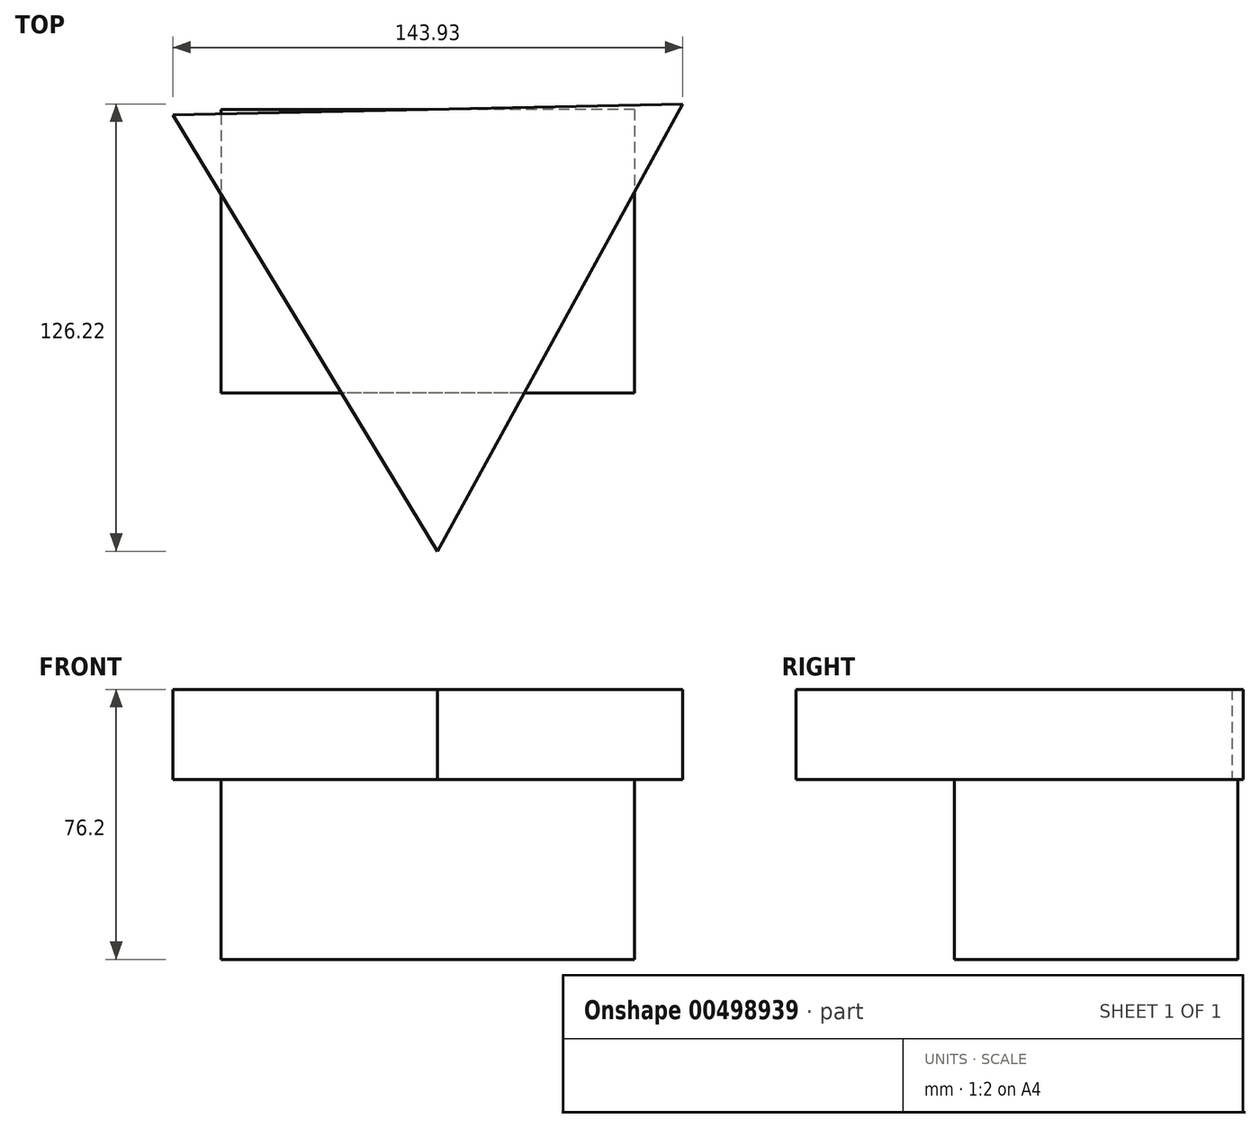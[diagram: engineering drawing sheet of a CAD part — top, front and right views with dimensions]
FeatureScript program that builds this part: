
annotation { "Feature Type Name" : "Feature", "Feature Type Description" : "" }
export const myFeature = defineFeature(function(context is Context, id is Id, definition is map)
    precondition{}
    {
        {
            var Q0;
            Q0=qCreatedBy(makeId("Top.planeOp"),FACE);
            var sketch = newSketch(context, id + "F0", { "sketchPlane" : qUnion([Q0])});
            skLineSegment(sketch, "E0.bottom", {"start": v(57.5, 41.55) * mm, "end": v(-59.3, 41.55) * mm});
            skLineSegment(sketch, "E0.top", {"start": v(57.5, -38.42) * mm, "end": v(-59.3, -38.42) * mm});
            skLineSegment(sketch, "E0.left", {"start": v(57.5, 41.55) * mm, "end": v(57.5, -38.42) * mm});
            skLineSegment(sketch, "E0.right", {"start": v(-59.3, 41.55) * mm, "end": v(-59.3, -38.42) * mm});
            skPoint(sketch, "E0.middle", {"position": v(-0.9, 1.57) * mm});
            skSolve(sketch);
        }
        {
            var Q0;
            Q0=makeQuery(id+"F0.imprint","IMPRINT",FACE,{"disambiguationData":[TD([[makeQuery(id+"F0.imprint","IMPRINT",EDGE,{"derivedFrom":sQuery(id+"F0.wireOp",EDGE,"E0.bottom")}),1.0]])]});
            extrude(context, id + "F1", {"entities" : qUnion([Q0]), "depth" : 50.8 * mm});
        }
        {
            var Q0;
            Q0=makeQuery(id+"F1.opExtrude","CAP_FACE",FACE,{"disambiguationData":[OSD([sQuery(id+"F0.wireOp",EDGE,"E0.bottom"),sQuery(id+"F0.wireOp",EDGE,"E0.top"),sQuery(id+"F0.wireOp",EDGE,"E0.left"),sQuery(id+"F0.wireOp",EDGE,"E0.right")])],"isStart":false});
            var sketch = newSketch(context, id + "F2", { "sketchPlane" : qUnion([Q0])});
            skCircle(sketch, "E1.cCircle", {"center": v(0, 0) * mm, "radius": 41.56 * mm, "construction": true});
            skLineSegment(sketch, "E1.0", {"start": v(-72.87, 39.98) * mm, "end": v(71.06, 43.12) * mm});
            skLineSegment(sketch, "E1.1", {"start": v(71.06, 43.12) * mm, "end": v(1.8, -83.1) * mm});
            skLineSegment(sketch, "E1.2", {"start": v(1.8, -83.1) * mm, "end": v(-72.87, 39.98) * mm});
            skPoint(sketch, "E1.0.midPoint", {"position": v(-0.9, 41.55) * mm});
            skSolve(sketch);
        }
        {
            var Q0;
            {var subQ0=sQuery(id+"F2.wireOp",EDGE,"E1.2");var subQ1=sQuery(id+"F2.wireOp",EDGE,"E1.1");var subQ2=makeQuery(id+"F2.imprint","INTERSECT",VERTEX,{"derivedFrom":[subQ1,subQ0]});Q0=makeQuery(id+"F2.imprint","IMPRINT",FACE,{"disambiguationData":[TD([[makeQuery(id+"F2.imprint","IMPRINT",EDGE,{"disambiguationData":[TD([[subQ2,1.0]])],"derivedFrom":subQ1}),-1.0]])]});}
            var Q1;
            {var subQ3=sQuery(id+"F2.wireOp",EDGE,"E1.0");var subQ8=makeQuery(id+"F1.opExtrude","CAP_EDGE",EDGE,{"disambiguationData":[OSD([sQuery(id+"F0.wireOp",EDGE,"E0.right")])],"isStart":false});var subQ10=makeQuery(id+"F2.imprint","INTERSECT",VERTEX,{"derivedFrom":[subQ8,subQ3]});Q1=makeQuery(id+"F2.imprint","IMPRINT",FACE,{"disambiguationData":[TD([[makeQuery(id+"F2.imprint","IMPRINT",EDGE,{"disambiguationData":[TD([[subQ10,-1.0]])],"derivedFrom":subQ3}),-1.0]])]});}
            var Q2;
            {var subQ0=sQuery(id+"F2.wireOp",EDGE,"E1.1");var subQ1=sQuery(id+"F2.wireOp",EDGE,"E1.0");var subQ2=makeQuery(id+"F2.imprint","INTERSECT",VERTEX,{"derivedFrom":[subQ1,subQ0]});Q2=makeQuery(id+"F2.imprint","IMPRINT",FACE,{"disambiguationData":[TD([[makeQuery(id+"F2.imprint","IMPRINT",EDGE,{"disambiguationData":[TD([[subQ2,1.0]])],"derivedFrom":subQ1}),-1.0]])]});}
            var Q3;
            {var subQ0=sQuery(id+"F2.wireOp",EDGE,"E1.2");var subQ1=sQuery(id+"F2.wireOp",EDGE,"E1.0");var subQ2=makeQuery(id+"F2.imprint","INTERSECT",VERTEX,{"derivedFrom":[subQ1,subQ0]});Q3=makeQuery(id+"F2.imprint","IMPRINT",FACE,{"disambiguationData":[TD([[makeQuery(id+"F2.imprint","IMPRINT",EDGE,{"disambiguationData":[TD([[subQ2,-1.0]])],"derivedFrom":subQ1}),-1.0]])]});}
            extrude(context, id + "F3", {"entities" : qUnion([Q0, Q1, Q2, Q3]), "operationType" : NewBodyOperationType.ADD, "depth" : 25.4 * mm, "offsetDistance" : 25.4 * mm});
        }
    });
